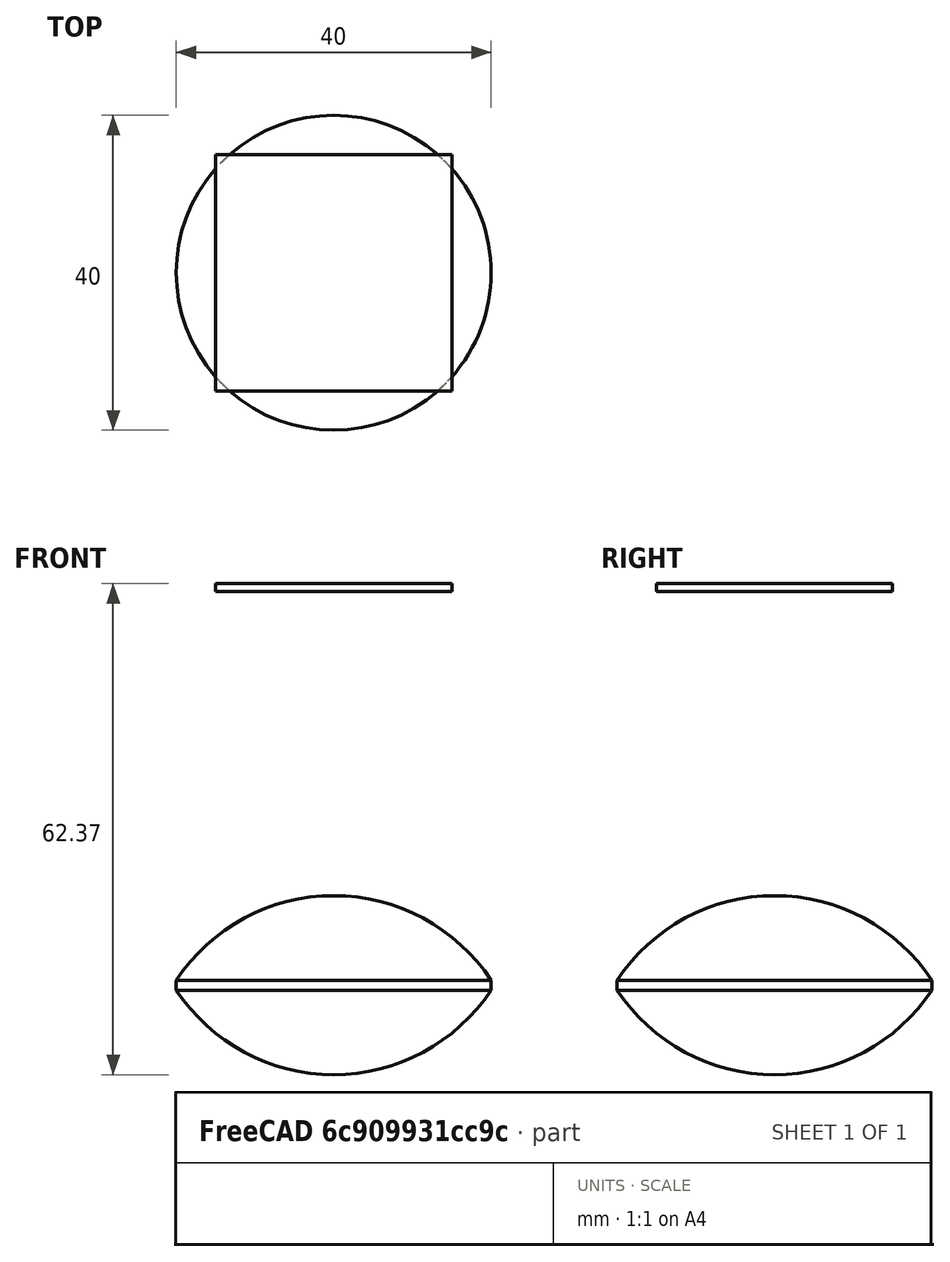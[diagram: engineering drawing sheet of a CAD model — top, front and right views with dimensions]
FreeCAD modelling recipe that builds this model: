
FCSTD DOCUMENT  (FreeCAD 1.1R44874 (Git))
Label: lens-optimizer
License: All rights reserved
LicenseURL: http://en.wikipedia.org/wiki/All_rights_reserved
objects: App::LinkGroupPython×3, Part::Sphere×2, Part::MultiCommon×2, Part::Box×1, Part::Cylinder×1, Part::FeaturePython×1
note: 7 computed .brp shape members not serialized (recipe doc carries the construction recipe); baked Part::Feature solids carry a one-line shape summary decoded from their .brp

FEATURE [Part::Sphere] Sphere
  Angle1 = -90
  Angle2 = 90
  Angle3 = 360
  AttacherType = Attacher::AttachEngine3D
  Placement = pos=(0,0,12.0677) rot=(0,0,1;0rad)
  Radius = 22.9286
FEATURE [Part::Sphere] Sphere001
  Angle1 = -90
  Angle2 = 90
  Angle3 = 360
  AttacherType = Attacher::AttachEngine3D
  Placement = pos=(0,0,-12.0677) rot=(0,0,1;0rad)
  Radius = 22.9286
FEATURE [Part::Box] Box001  label="Cube001"
  AttacherType = Attacher::AttachEngine3D
  Height = 1
  Length = 30
  Placement = pos=(-15,-15,0) rot=(0,0,1;0rad)
  Width = 30
FEATURE [Part::Cylinder] Cylinder
  Angle = 360
  AttacherType = Attacher::AttachEngine3D
  FirstAngle = 0
  Height = 200
  Placement = pos=(0,0,-100) rot=(0,0,1;0rad)
  Radius = 20
  SecondAngle = 0
FEATURE [Part::MultiCommon] Common
  Behavior = 1
  Shapes = -> [Sphere,Sphere001]
FEATURE [Part::MultiCommon] Common001
  Behavior = 1
  Placement = pos=(0,0,-50) rot=(0,0,1;0rad)
  Shapes = -> [Common,Cylinder]
FEATURE [App::LinkGroupPython] OpticalPointSource001  # WARN: FeaturePython — macro-defined, semantics opaque (R4)
  Divergence = -
  FanPhi0 = 0
  Fans = 2
  FocalLength = 0
  LinkMode = 0
  MaxIntersectionsScale = 1
  MaxRayLengthScale = 1
  PhiDomain = 0, 2*pi
  PhiResolutionNumericMode = 3
  Placement = pos=(0,0,-74) rot=(0,0,1;0rad)
  PowerDensity = exp(-theta^2/0.01)
  RadiusDomain = 0, 10
  RadiusResolutionNumericMode = 1000000
  RandomNumberGeneratorMode = ?
  RaysPerFan = 20
  RaysPerIterationScale = 1
  RecordRays = false
  ThetaDomain = 0, pi/4
  ThetaResolutionNumericMode = 1000000
  Wavelength = 500
FEATURE [App::LinkGroupPython] OpticalLensGroup  # WARN: FeaturePython — macro-defined, semantics opaque (R4)
  AbsorptionLength = inf
  ElementList = -> [Common001]
  GratingDiffractionOrder = 1
  GratingLinesOrientation = (0,0,1)
  GratingLinesPerMillimeter = 1000
  GratingType = 0
  LinkMode = 0
  ModifyPhiDomain = 0, 2*pi
  ModifyThetaDomain = -pi/2, pi/2
  OpticalType = 1
  PowerPhiDomain = 0, 2*pi
  PowerThetaDomain = -pi/2, pi/2
  RayModificationProbabilityDensity = DiracDelta(theta)
  RecordHits = false
  ReflectedPowerDensity = DiracDelta(theta-theta_refl) * DiracDelta(phi-phi_refl)
  Reflectivity = 1
  RefractiveIndex = 2
FEATURE [Part::FeaturePython] OpticalSimulationSettings  # WARN: FeaturePython — macro-defined, semantics opaque (R4)
  Active = true
  DistanceTolerance = 0.01
  EnableStoreSingleShotData = false
  EndAfterHits = inf
  EndAfterIterations = inf
  EndAfterRays = 1000
  MaxIntersections = 100
  MaxRayLength = 1000
  RaysPerIteration = 100
  SequentialMode = false
  ShowRaysInContinuousMode = true
  StoreHitFanIndex = false
  StoreHitInitDirection = false
  StoreHitInitPhi = false
  StoreHitInitPoint = false
  StoreHitInitPower = false
  StoreHitInitTheta = false
  StoreHitInitWavelength = false
  StoreHitRayIndex = false
  StoreHitTotalFanCount = false
  StoreHitTotalRaysInFan = false
  WorkerProcessCount = num_cpus
FEATURE [App::LinkGroupPython] OpticalAbsorberGroup  # WARN: FeaturePython — macro-defined, semantics opaque (R4)
  AbsorptionLength = inf
  ElementList = -> [Box001]
  GratingDiffractionOrder = 1
  GratingLinesOrientation = (0,0,1)
  GratingLinesPerMillimeter = 1000
  GratingType = 0
  LinkMode = 0
  ModifyPhiDomain = 0, 2*pi
  ModifyThetaDomain = -pi/2, pi/2
  OpticalType = 3
  PowerPhiDomain = 0, 2*pi
  PowerThetaDomain = -pi/2, pi/2
  RayModificationProbabilityDensity = DiracDelta(theta)
  RecordHits = true
  ReflectedPowerDensity = DiracDelta(theta-theta_refl) * DiracDelta(phi-phi_refl)
  Reflectivity = 1
  RefractiveIndex = 2
